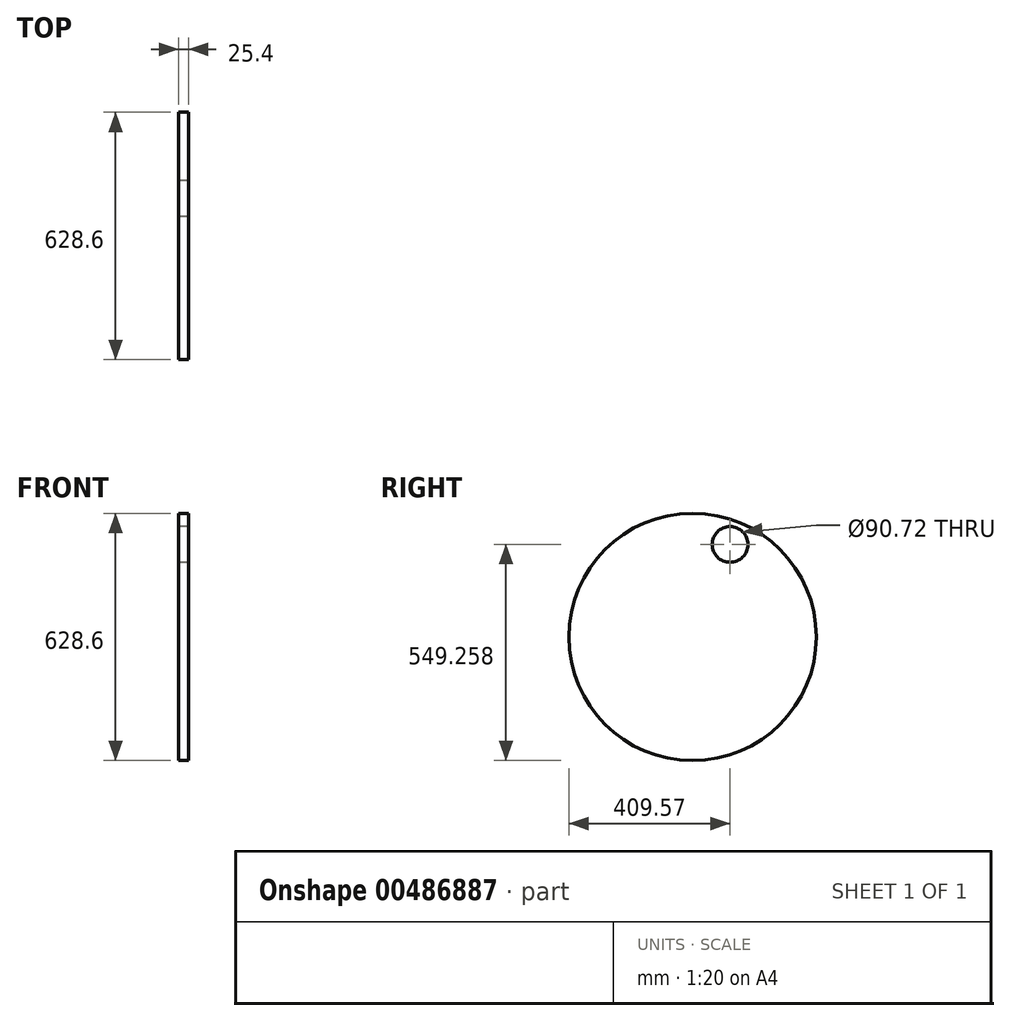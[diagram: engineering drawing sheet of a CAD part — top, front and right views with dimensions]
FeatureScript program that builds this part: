
annotation { "Feature Type Name" : "Feature", "Feature Type Description" : "" }
export const myFeature = defineFeature(function(context is Context, id is Id, definition is map)
    precondition{}
    {
        {
            var Q0;
            Q0=qCreatedBy(makeId("Right.planeOp"),FACE);
            var sketch = newSketch(context, id + "F0", { "sketchPlane" : qUnion([Q0])});
            skCircle(sketch, "E0", {"center": v(71.01, 40.12) * mm, "radius": 45.36 * mm});
            skPoint(sketch, "E0.first.point", {"position": v(49.84, 0) * mm});
            skPoint(sketch, "E0.second.point", {"position": v(66.13, 85.22) * mm});
            skPoint(sketch, "E0.third.point", {"position": v(114.9, 51.56) * mm});
            skCircle(sketch, "E1", {"center": v(-24.26, -194.84) * mm, "radius": 314.3 * mm});
            skPoint(sketch, "E1.first.point", {"position": v(10.8, 117.5) * mm});
            skPoint(sketch, "E1.second.point", {"position": v(-42.9, 118.9) * mm});
            skPoint(sketch, "E1.third.point", {"position": v(58.8, 108.28) * mm});
            skSolve(sketch);
        }
        {
            var Q0;
            Q0 = qSketchRegion(id + "F0", true);
            extrude(context, id + "F1", {"entities" : qUnion([Q0]), "depth" : 25.4 * mm});
        }
    });
